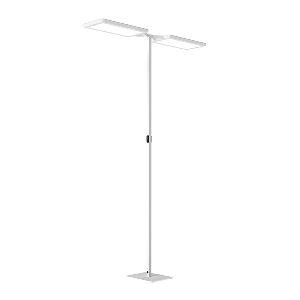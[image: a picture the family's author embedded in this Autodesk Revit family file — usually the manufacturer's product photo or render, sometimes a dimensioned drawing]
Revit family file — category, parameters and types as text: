
# Revit family: yara_doublet_-_yts_2_15000_vtl_r_ws_cee_s0_c_114268000-00808495_1b8a
name_source: partatom
category: Lighting Fixtures
units: mm (PartAtom-declared; Revit-internal decimal feet)

## family parameters
Cut with Voids When Loaded = No
Host = Face
Light Source = No
Part Type = Normal
Room Calculation Point = No
Round Connector Dimension = Use Diameter
Shared = No

## types (1)
- YARA.doubleT - YTS 2/15000/VTL/R/WS/CEE/S0/C (1 x LED, 15000 lm, VTL)
    Apparent Load = 214 VA
    Approval mark = CE
    CIE Flux Codes = 58 87 97 13 100
    Color Rendering = 80-89
    Color Temperature = VTL
    Control Gear = Electronic ballast
    Default Elevation = 1800 mm
    Description = YTS 2/15000/VTL/R/WS/CEE/S0/R|Free-standing luminaire|light source: LED|work equipment: Electronic ballast DALI|connected load: 220-240 V, 50/60 Hz|Power consumption: approx. 210 W|power factor: approx. 0,966|luminous flux: 30000 lm|luminous efficacy: 142 lm/W|light distribution: Direct/indirect|direct ratio: approx. 13 %|colour temperature: Daylight, ca. 2700-6500 K|color rendering index (CRI): >= 80|chromaticity tolerance:  3 SDCM|technology: Presence and daylight sensor control (PIR)|operation: Wireless switch|luminaire body|material: Aluminium/plastic|surface: Powder coatet|colour: White|lamp cover: Acrylic (PMMA), Satine, Structured|tubular section|material: Steel tube|surface: Powder-coated|Form: Tubular section upright|colour of tubular section: White|luminaire base|Form: Rectangular flat|weight (net): approx. 24.0 kg|mains lead: 3.00 m Mains plug CEE 7/VII|Fastening: Floor standing base|glare control: Conical prismatic screen|luminance(L65): <= 2700 cd/m|unified glare rating(4H 8H): <=  16|special features: App control, Asymmetric radiation, Biodynamic light VTL, Direct and indirect lighting component with edge light and light guidetechnology for a homogeneous light exit, Flicker-free, Magnetic control panel, freely positionable, PIR movement and daylight sensor, TALK Bluetooth|Approval mark: VDE - ENEC|
    Frequency = 50 Hz, 60 Hz
    Height = 24 mm  [stored 0.0787402 ft]
    Lamp = 1 x LED
    Lamp Light Flux = 15000 lm
    Lamp count = 1
    Length = 690 mm
    Luminous efficacy = 140 lm/W
    Manufacturer = Waldmann
    ModVariant = No
    Model = 114268000-00808495
    Mounting Place = Floor
    Mounting Type = Freestanding
    Number of Poles = 1
    OnlyDefault = Yes
    Power Factor = 1
    Product Name = YARA.doubleT - YTS 2/15000/VTL/R/WS/CEE/S0/C
    Product group = Free standing luminaire
    ProductGroupID = 13
    Protection Class = Protection class I
    Protection Degree = IP 20
    RLX_Detail_Level = 1
    RlxData = <blob elided: 62637 chars, md5=bdfa5e39>
    Socket = socket
    Standby Power = 0 W
    System Light Flux = 30000 lm
    System Power = 214 W
    Type Comments = Product without accessories
    Type Image = yts-r-ws-r.jpg
    URL = http://relux.com
    VarID = ---
    Voltage = 230 V
    Voltage Range = 220-240 V
    Weight = 0.00 kg
    Width = 358 mm

note: [stored X ft] marks values corroborated as IEEE doubles in the binary element streams (Revit-internal decimal feet)

## geometry (parser evidence)
native form markers: Blend x4, Sweep x15
no freeform markers — native parametric forms only
